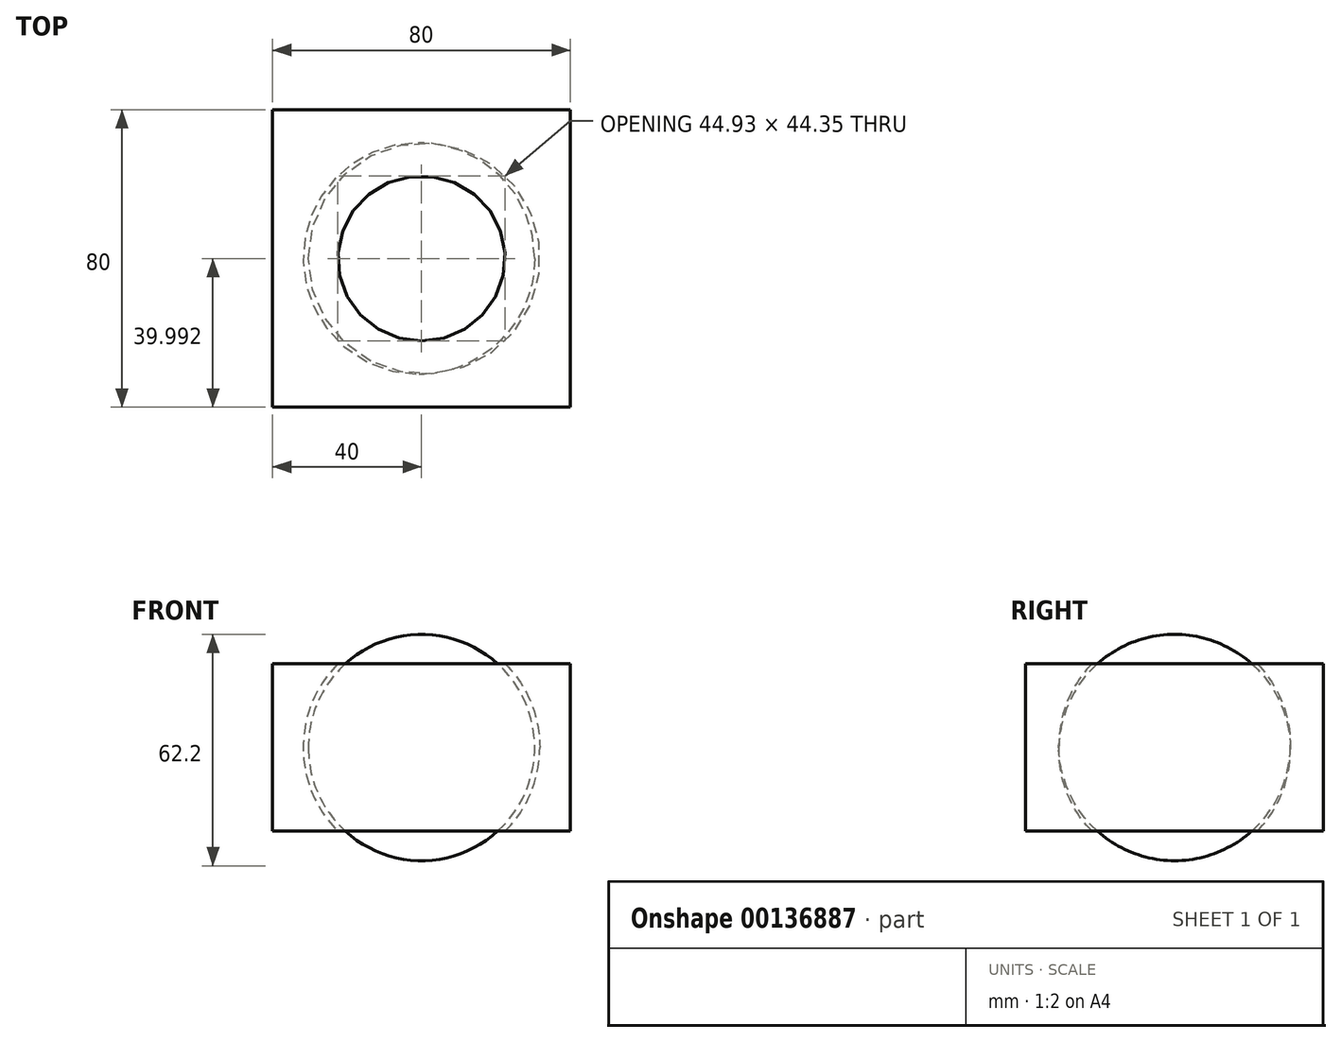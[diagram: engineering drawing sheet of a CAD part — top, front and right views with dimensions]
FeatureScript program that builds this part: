
annotation { "Feature Type Name" : "Feature", "Feature Type Description" : "" }
export const myFeature = defineFeature(function(context is Context, id is Id, definition is map)
    precondition{}
    {
        {
            var Q0;
            Q0=qCreatedBy(makeId("Top.planeOp"),FACE);
            var sketch = newSketch(context, id + "F0", { "sketchPlane" : qUnion([Q0])});
            skLineSegment(sketch, "E0.bottom", {"start": v(40, 40) * mm, "end": v(-40, 40) * mm});
            skLineSegment(sketch, "E0.top", {"start": v(40, -40) * mm, "end": v(-40, -40) * mm});
            skLineSegment(sketch, "E0.left", {"start": v(40, 40) * mm, "end": v(40, -40) * mm});
            skLineSegment(sketch, "E0.right", {"start": v(-40, 40) * mm, "end": v(-40, -40) * mm});
            skPoint(sketch, "E0.middle", {"position": v(0, 0) * mm});
            skSolve(sketch);
        }
        {
            var Q0;
            Q0 = qSketchRegion(id + "F0", true);
            extrude(context, id + "F1", {"entities" : qUnion([Q0]), "endBound" : BoundingType.SYMMETRIC, "depth" : 45 * mm});
        }
        {
            var Q0;
            Q0=qCreatedBy(makeId("Top.planeOp"),FACE);
            var sketch = newSketch(context, id + "F2", { "sketchPlane" : qUnion([Q0])});
            skLineSegment(sketch, "E1", {"start": v(0, 31.08) * mm, "end": v(0, -31.1) * mm});
            skArc(sketch, "E2", {"start": v(0, -31.1) * mm, "mid": v(31.8, 0) * mm, "end": v(0, 31.08) * mm});
            skSolve(sketch);
        }
        {
            var Q0;
            Q0=makeQuery(id+"F2.imprint","IMPRINT",FACE,{"disambiguationData":[TD([[makeQuery(id+"F2.imprint","IMPRINT",EDGE,{"derivedFrom":sQuery(id+"F2.wireOp",EDGE,"E1")}),1.0]])]});
            var Q1;
            Q1=sQuery(id+"F2.wireOp",EDGE,"E1");
            revolve(context, id + "F3", {"operationType" : NewBodyOperationType.REMOVE, "entities" : qUnion([Q0]), "axis" : qUnion([Q1]), "revolveType" : RevolveType.FULL, "oppositeDirection" : true});
        }
    });
